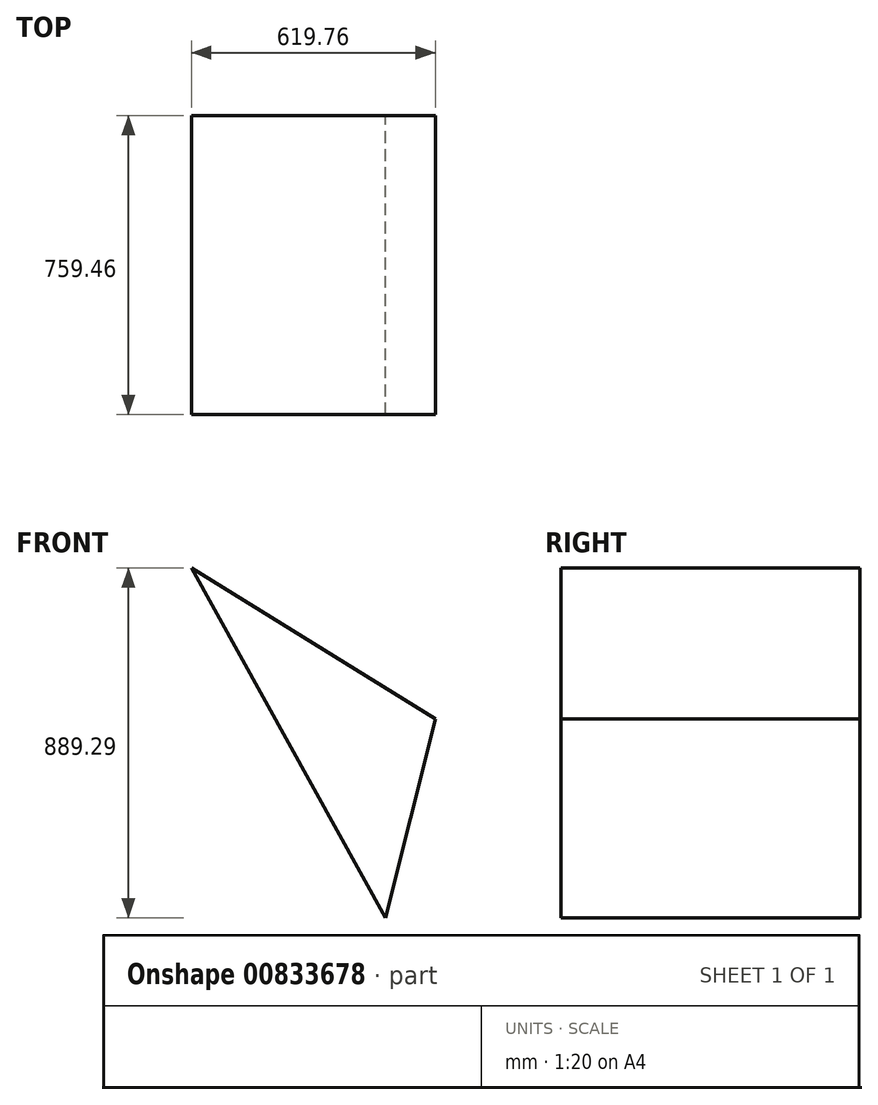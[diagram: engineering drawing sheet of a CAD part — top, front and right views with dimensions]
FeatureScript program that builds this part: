
annotation { "Feature Type Name" : "Feature", "Feature Type Description" : "" }
export const myFeature = defineFeature(function(context is Context, id is Id, definition is map)
    precondition{}
    {
        {
            var Q0;
            Q0=qCreatedBy(makeId("Front.planeOp"),FACE);
            var sketch = newSketch(context, id + "F0", { "sketchPlane" : qUnion([Q0])});
            skLineSegment(sketch, "E0", {"start": v(-492.76, 485.98) * mm, "end": v(127, 102.7) * mm});
            skLineSegment(sketch, "E1", {"start": v(127, 102.7) * mm, "end": v(0, -403.31) * mm});
            skLineSegment(sketch, "E2", {"start": v(0, -403.31) * mm, "end": v(-492.76, 485.98) * mm});
            skSolve(sketch);
        }
        {
            var Q0;
            Q0 = qSketchRegion(id + "F0", true);
            extrude(context, id + "F1", {"entities" : qUnion([Q0]), "depth" : 759.46 * mm, "offsetDistance" : 25.4 * mm});
        }
    });
